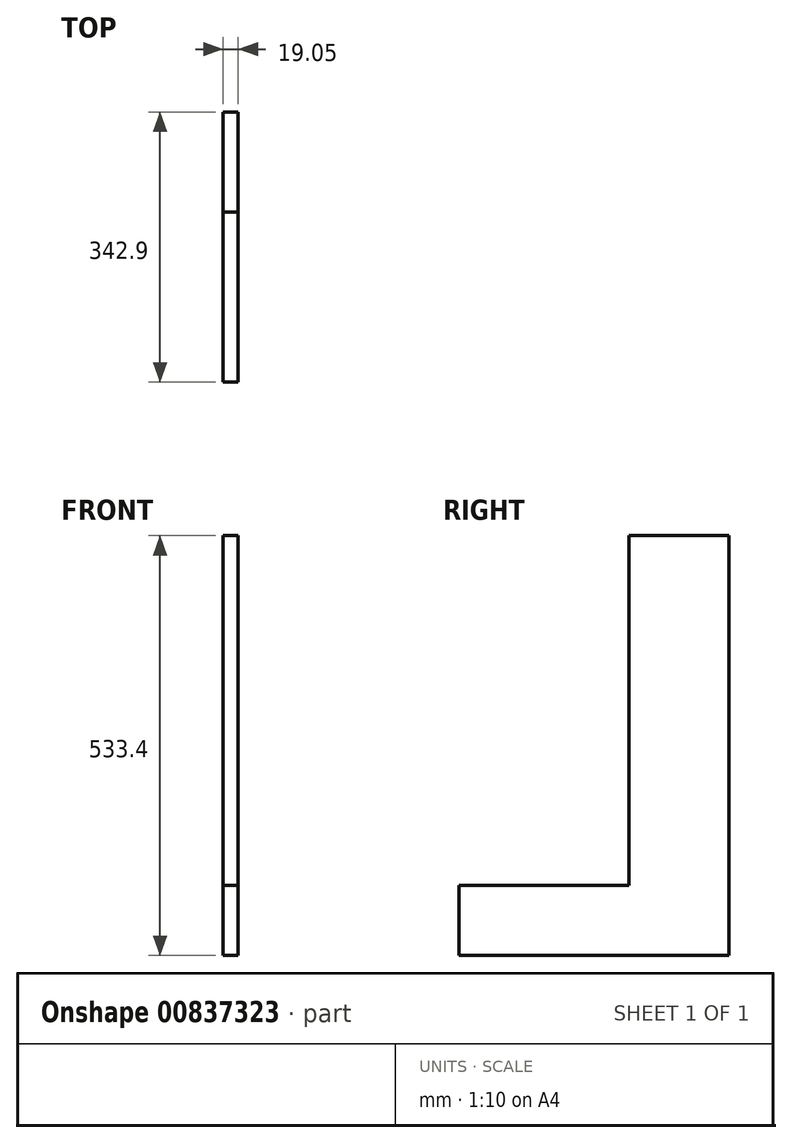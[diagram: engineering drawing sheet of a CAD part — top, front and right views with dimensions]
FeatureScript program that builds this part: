
annotation { "Feature Type Name" : "Feature", "Feature Type Description" : "" }
export const myFeature = defineFeature(function(context is Context, id is Id, definition is map)
    precondition{}
    {
        {
            var Q0;
            Q0=qCreatedBy(makeId("Right.planeOp"),FACE);
            var sketch = newSketch(context, id + "F0", { "sketchPlane" : qUnion([Q0])});
            skLineSegment(sketch, "E0", {"start": v(0, 0) * mm, "end": v(0, 533.4) * mm});
            skLineSegment(sketch, "E1", {"start": v(0, 533.4) * mm, "end": v(-127, 533.4) * mm});
            skLineSegment(sketch, "E2", {"start": v(-342.9, 88.9) * mm, "end": v(-342.9, 0) * mm});
            skLineSegment(sketch, "E3", {"start": v(-342.9, 0) * mm, "end": v(0, 0) * mm});
            skLineSegment(sketch, "E4", {"start": v(-342.9, 88.9) * mm, "end": v(-127, 88.9) * mm});
            skLineSegment(sketch, "E5", {"start": v(-127, 88.9) * mm, "end": v(-127, 533.4) * mm});
            skSolve(sketch);
        }
        {
            var Q0;
            Q0=makeQuery(id+"F0.imprint","IMPRINT",FACE,{"disambiguationData":[TD([[makeQuery(id+"F0.imprint","IMPRINT",EDGE,{"derivedFrom":sQuery(id+"F0.wireOp",EDGE,"E0")}),1.0]])]});
            extrude(context, id + "F1", {"entities" : qUnion([Q0]), "depth" : 19.05 * mm, "offsetDistance" : 25.4 * mm});
        }
    });
